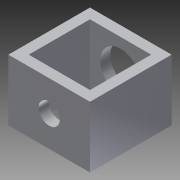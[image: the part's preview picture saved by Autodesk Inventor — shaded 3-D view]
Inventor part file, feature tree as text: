
AUTODESK INVENTOR PART (.ipt)
format: ipt  version: 2013 (Build 170138000, 138)  size: 100,864 bytes
history: native  units: in
note: dims shown in document units (in); Inventor stores cm internally (conversion verified against a paired STEP export)
features: extrude x3, sketch x3
ambient origin geometry x8: Origin, YZ Plane, XZ Plane, XY Plane, X Axis, Y Axis, Z Axis, Center Point
bodies: Solid1 (feature_tree)
feature tree (6):
  extrude  "Extrusion1"  Depth=1.0in
  extrude  "Extrusion2"  Depth=0.75in TaperAngle=0.0deg
  extrude  "Extrusion3"  Depth=1.0in TaperAngle=0.0deg
  sketch  "Sketch1"  dims[d0=1.0in d1=1.0in]
  sketch  "Sketch2"  dims[d2=0.125in d3=0.75in d4=0.0in]
  sketch  "Sketch3"  dims[d5=0.26in d7=1.0in d8=0.0in d9=0.5in d11=0.125in d12=0.0in]
